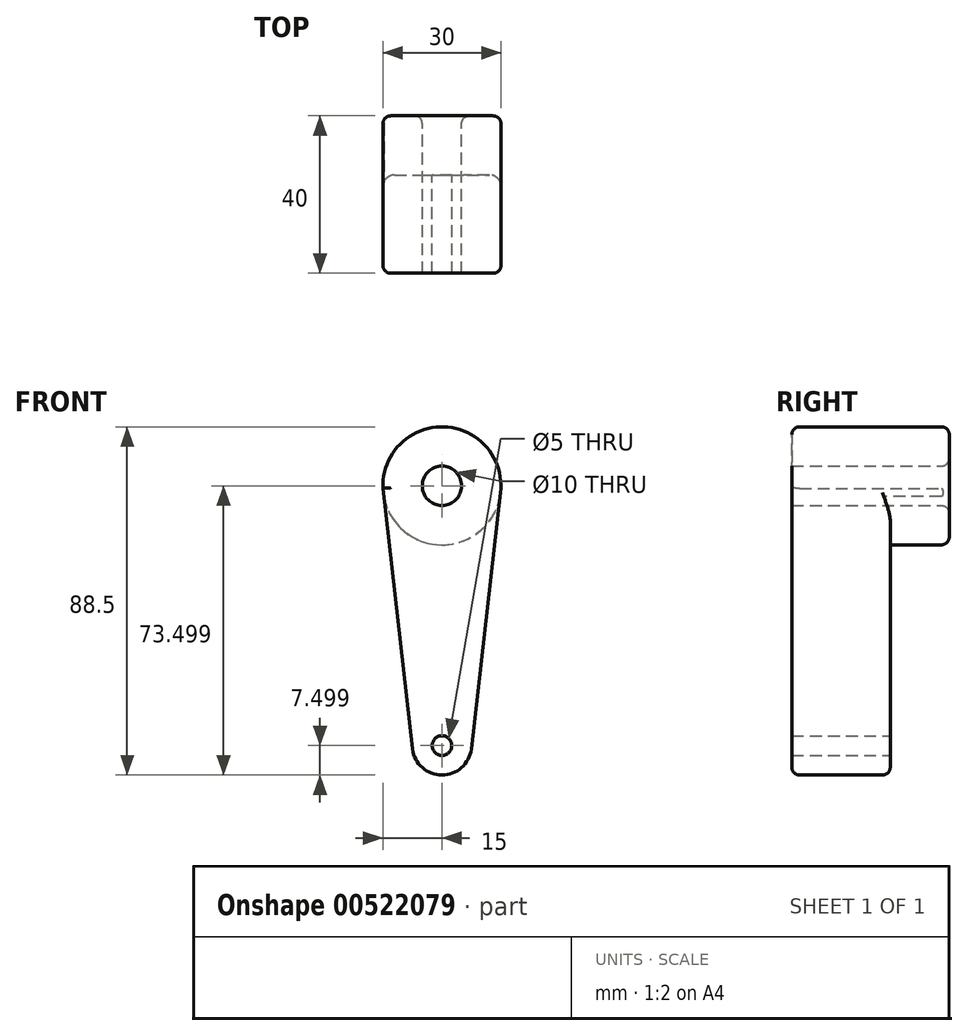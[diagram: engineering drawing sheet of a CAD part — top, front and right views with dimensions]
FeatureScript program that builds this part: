
annotation { "Feature Type Name" : "Feature", "Feature Type Description" : "" }
export const myFeature = defineFeature(function(context is Context, id is Id, definition is map)
    precondition{}
    {
        {
            var Q0;
            Q0=qCreatedBy(makeId("Front.planeOp"),FACE);
            var sketch = newSketch(context, id + "F0", { "sketchPlane" : qUnion([Q0])});
            skCircle(sketch, "E0", {"center": v(0, 12.38) * mm, "radius": 15 * mm});
            skCircle(sketch, "E1", {"center": v(0, -53.62) * mm, "radius": 7.5 * mm});
            skCircle(sketch, "E2", {"center": v(0, 12.38) * mm, "radius": 5 * mm});
            skCircle(sketch, "E3", {"center": v(0, -53.62) * mm, "radius": 2.5 * mm});
            skLineSegment(sketch, "E4", {"start": v(14.9, 10.63) * mm, "end": v(7.45, -54.47) * mm});
            skLineSegment(sketch, "E5", {"start": v(-14.99, 11.74) * mm, "end": v(-7.45, -54.47) * mm});
            skSolve(sketch);
        }
        {
            var Q0;
            {var subQ0=sQuery(id+"F0.wireOp",EDGE,"E4");Q0=makeQuery(id+"F0.imprint","IMPRINT",FACE,{"disambiguationData":[TD([[makeQuery(id+"F0.imprint","IMPRINT",EDGE,{"derivedFrom":subQ0}),-1.0]])]});}
            var Q1;
            Q1=makeQuery(id+"F0.imprint","IMPRINT",FACE,{"disambiguationData":[TD([[makeQuery(id+"F0.imprint","IMPRINT",EDGE,{"derivedFrom":sQuery(id+"F0.wireOp",EDGE,"E2")}),-1.0]])]});
            var Q2;
            Q2=makeQuery(id+"F0.imprint","IMPRINT",FACE,{"disambiguationData":[TD([[makeQuery(id+"F0.imprint","IMPRINT",EDGE,{"derivedFrom":sQuery(id+"F0.wireOp",EDGE,"E3")}),-1.0]])]});
            extrude(context, id + "F1", {"entities" : qUnion([Q0, Q1, Q2]), "depth" : 25 * mm, "offsetDistance" : 25 * mm});
        }
        {
            var Q0;
            Q0=makeQuery(id+"F0.imprint","IMPRINT",FACE,{"disambiguationData":[TD([[makeQuery(id+"F0.imprint","IMPRINT",EDGE,{"derivedFrom":sQuery(id+"F0.wireOp",EDGE,"E2")}),-1.0]])]});
            extrude(context, id + "F2", {"entities" : qUnion([Q0]), "operationType" : NewBodyOperationType.ADD, "oppositeDirection" : true, "depth" : 15 * mm, "offsetDistance" : 25 * mm});
        }
        {
            var Q0;
            Q0=makeQuery(id+"F2.opExtrude","CAP_EDGE",EDGE,{"disambiguationData":[OSD([sQuery(id+"F0.wireOp",EDGE,"E0")])],"isStart":false});
            var Q1;
            Q1=makeQuery(id+"F2.opExtrude","CAP_EDGE",EDGE,{"disambiguationData":[OSD([sQuery(id+"F0.wireOp",EDGE,"E2")])],"isStart":false});
            var Q2;
            Q2=makeQuery(id+"F1.opExtrude","CAP_EDGE",EDGE,{"disambiguationData":[OSD([sQuery(id+"F0.wireOp",EDGE,"E1")])],"isStart":true});
            var Q3;
            Q3=makeQuery(id+"F1.opExtrude","CAP_EDGE",EDGE,{"disambiguationData":[OSD([sQuery(id+"F0.wireOp",EDGE,"E4")])],"isStart":false});
            var Q4;
            Q4=makeQuery(id+"F1.opExtrude","CAP_EDGE",EDGE,{"disambiguationData":[OSD([sQuery(id+"F0.wireOp",EDGE,"E0")])],"isStart":false});
            var Q5;
            Q5=makeQuery(id+"F1.opExtrude","CAP_EDGE",EDGE,{"disambiguationData":[OSD([sQuery(id+"F0.wireOp",EDGE,"E1")])],"isStart":false});
            fillet(context, id + "F3", {"entities" : qUnion([Q0, Q1, Q2, Q3, Q4, Q5]), "radius" : 2 * mm, "tangentPropagation" : true, "allowEdgeOverflow" : false});
        }
    });
